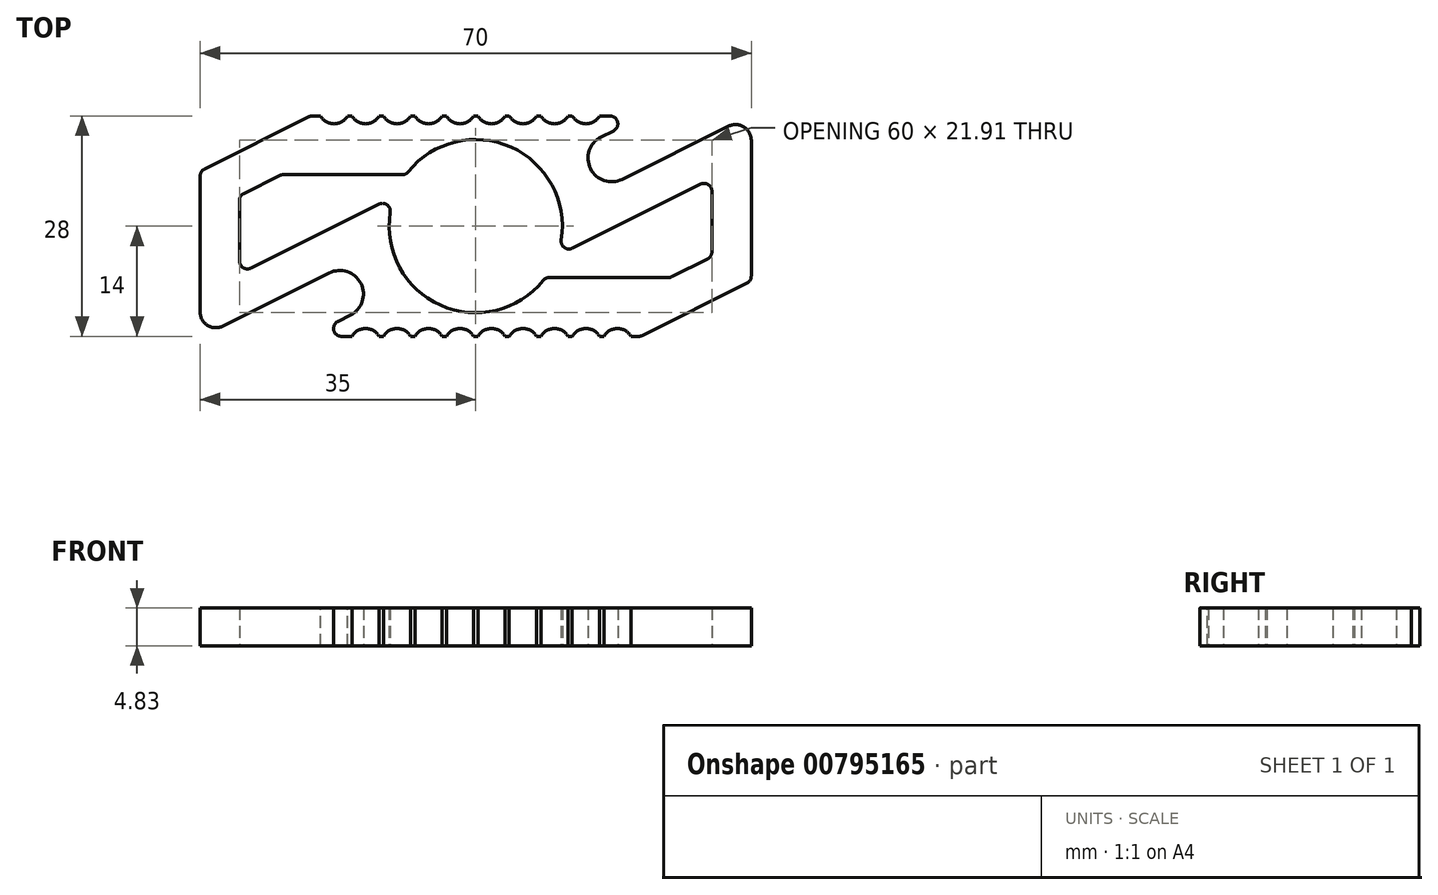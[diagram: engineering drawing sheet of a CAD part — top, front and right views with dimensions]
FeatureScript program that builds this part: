
annotation { "Feature Type Name" : "Feature", "Feature Type Description" : "" }
export const myFeature = defineFeature(function(context is Context, id is Id, definition is map)
    precondition{}
    {
        {
            var Q0;
            Q0=qCreatedBy(makeId("Top.planeOp"),FACE);
            var sketch = newSketch(context, id + "F0", { "sketchPlane" : qUnion([Q0])});
            skArc(sketch, "E0", {"start": v(-10.86, 1.74) * mm, "mid": v(-8.37, -7.14) * mm, "end": v(0, -11) * mm});
            skLineSegment(sketch, "E1.bottom", {"start": v(0, -14) * mm, "end": v(-17.06, -14) * mm});
            skLineSegment(sketch, "E1.top", {"start": v(0, 14) * mm, "end": v(-20.72, 14) * mm});
            skLineSegment(sketch, "E1.right", {"start": v(-35, -10.9) * mm, "end": v(-35, 6.36) * mm});
            skLineSegment(sketch, "E2", {"start": v(0, 29.38) * mm, "end": v(0, -31.46) * mm, "construction": true});
            skLineSegment(sketch, "E3", {"start": v(-17.27, -8.63) * mm, "end": v(-28, -14) * mm});
            skArc(sketch, "E4.0.startCap", {"start": v(-18.6, -5.95) * mm, "mid": v(-14.58, -7.3) * mm, "end": v(-15.93, -11.32) * mm});
            skLineSegment(sketch, "E4.0.left", {"start": v(-15.93, -11.32) * mm, "end": v(-17.5, -12.1) * mm});
            skLineSegment(sketch, "E4.0.right", {"start": v(-18.6, -5.95) * mm, "end": v(-32.1, -12.7) * mm});
            skLineSegment(sketch, "E5.trimOffspring", {"start": v(-34.7, -14) * mm, "end": v(-35, -14) * mm});
            skArc(sketch, "E6.filletArc", {"start": v(-35, -10.9) * mm, "mid": v(-34.05, -12.61) * mm, "end": v(-32.1, -12.7) * mm});
            skPoint(sketch, "E7.visualSharp", {"position": v(-21.3, -14) * mm});
            skArc(sketch, "E7.filletArc", {"start": v(-17.5, -12.1) * mm, "mid": v(-18.03, -13.23) * mm, "end": v(-17.06, -14) * mm});
            skLineSegment(sketch, "E8.0.right", {"start": v(-21.17, 13.9) * mm, "end": v(-34.45, 7.26) * mm});
            skLineSegment(sketch, "E9.3", {"start": v(-24.93, 6.42) * mm, "end": v(-29.45, 4.17) * mm});
            skLineSegment(sketch, "E9.4", {"start": v(-30, -4.44) * mm, "end": v(-30, 3.27) * mm});
            skLineSegment(sketch, "E9.5", {"start": v(-12.3, 2.8) * mm, "end": v(-28.55, -5.33) * mm});
            skPoint(sketch, "E10.visualSharp", {"position": v(-30, 3.89) * mm});
            skArc(sketch, "E10.filletArc", {"start": v(-29.45, 4.17) * mm, "mid": v(-29.85, 3.8) * mm, "end": v(-30, 3.27) * mm});
            skPoint(sketch, "E11.visualSharp", {"position": v(-30, -6.06) * mm});
            skArc(sketch, "E11.filletArc", {"start": v(-30, -4.44) * mm, "mid": v(-29.53, -5.29) * mm, "end": v(-28.55, -5.33) * mm});
            skPoint(sketch, "E12.visualSharp", {"position": v(-19.78, 9) * mm});
            skArc(sketch, "E13.trimOffspring", {"start": v(0, 11) * mm, "mid": v(-4.75, 9.92) * mm, "end": v(-8.56, 6.9) * mm});
            skPoint(sketch, "E14.visualSharp", {"position": v(-35, 6.98) * mm});
            skArc(sketch, "E14.filletArc", {"start": v(-34.45, 7.26) * mm, "mid": v(-34.85, 6.89) * mm, "end": v(-35, 6.36) * mm});
            skLineSegment(sketch, "E15.1.0", {"start": v(21.17, -13.9) * mm, "end": v(34.45, -7.26) * mm});
            skLineSegment(sketch, "E15.1.1", {"start": v(30, 4.44) * mm, "end": v(30, -3.27) * mm});
            skPoint(sketch, "E15.1.2", {"position": v(19.78, -9) * mm});
            skLineSegment(sketch, "E15.1.3", {"start": v(24.93, -6.42) * mm, "end": v(29.45, -4.17) * mm});
            skPoint(sketch, "E15.1.4", {"position": v(35, -6.98) * mm});
            skLineSegment(sketch, "E15.1.5", {"start": v(15.93, 11.32) * mm, "end": v(17.5, 12.1) * mm});
            skLineSegment(sketch, "E15.1.6", {"start": v(18.6, 5.95) * mm, "end": v(32.1, 12.7) * mm});
            skLineSegment(sketch, "E15.1.8", {"start": v(12.3, -2.8) * mm, "end": v(28.55, 5.33) * mm});
            skArc(sketch, "E15.1.9", {"start": v(0, -11) * mm, "mid": v(4.75, -9.92) * mm, "end": v(8.56, -6.9) * mm});
            skArc(sketch, "E15.1.10", {"start": v(18.6, 5.95) * mm, "mid": v(14.58, 7.3) * mm, "end": v(15.93, 11.32) * mm});
            skPoint(sketch, "E15.1.11", {"position": v(30, 6.06) * mm});
            skLineSegment(sketch, "E15.1.12", {"start": v(17.27, 8.63) * mm, "end": v(28, 14) * mm});
            skLineSegment(sketch, "E15.1.13", {"start": v(35, 10.9) * mm, "end": v(35, -6.36) * mm});
            skLineSegment(sketch, "E15.1.15", {"start": v(0, -14) * mm, "end": v(20.72, -14) * mm});
            skLineSegment(sketch, "E15.1.16", {"start": v(0, 14) * mm, "end": v(17.06, 14) * mm});
            skArc(sketch, "E15.1.17", {"start": v(10.86, -1.74) * mm, "mid": v(8.37, 7.14) * mm, "end": v(0, 11) * mm});
            skPoint(sketch, "E15.1.18", {"position": v(21.3, 14) * mm});
            skPoint(sketch, "E15.1.19", {"position": v(30, -3.89) * mm});
            skArc(sketch, "E15.1.20", {"start": v(35, 10.9) * mm, "mid": v(34.05, 12.61) * mm, "end": v(32.1, 12.7) * mm});
            skLineSegment(sketch, "E15.1.21", {"start": v(34.7, 14) * mm, "end": v(35, 14) * mm});
            skArc(sketch, "E15.1.22", {"start": v(30, 4.44) * mm, "mid": v(29.53, 5.29) * mm, "end": v(28.55, 5.33) * mm});
            skArc(sketch, "E15.1.23", {"start": v(17.5, 12.1) * mm, "mid": v(18.03, 13.23) * mm, "end": v(17.06, 14) * mm});
            skArc(sketch, "E15.1.24", {"start": v(29.45, -4.17) * mm, "mid": v(29.85, -3.8) * mm, "end": v(30, -3.27) * mm});
            skArc(sketch, "E15.1.25", {"start": v(34.45, -7.26) * mm, "mid": v(34.85, -6.89) * mm, "end": v(35, -6.36) * mm});
            skPoint(sketch, "E16.visualSharp", {"position": v(-10.33, 3.78) * mm});
            skArc(sketch, "E16.filletArc", {"start": v(-10.86, 1.74) * mm, "mid": v(-11.26, 2.7) * mm, "end": v(-12.3, 2.8) * mm});
            skPoint(sketch, "E17.visualSharp", {"position": v(10.33, -3.78) * mm});
            skArc(sketch, "E17.filletArc", {"start": v(10.86, -1.74) * mm, "mid": v(11.26, -2.7) * mm, "end": v(12.3, -2.8) * mm});
            skPoint(sketch, "E18.visualSharp", {"position": v(6.32, -9) * mm});
            skPoint(sketch, "E19.visualSharp", {"position": v(-6.32, 9) * mm});
            skPoint(sketch, "E20.visualSharp", {"position": v(-20.96, 14) * mm});
            skArc(sketch, "E20.filletArc", {"start": v(-20.72, 14) * mm, "mid": v(-20.95, 13.97) * mm, "end": v(-21.17, 13.9) * mm});
            skPoint(sketch, "E21.visualSharp", {"position": v(20.96, -14) * mm});
            skArc(sketch, "E21.filletArc", {"start": v(20.72, -14) * mm, "mid": v(20.95, -13.97) * mm, "end": v(21.17, -13.9) * mm});
            skLineSegment(sketch, "E22", {"start": v(-24.48, 6.53) * mm, "end": v(-9.34, 6.53) * mm});
            skLineSegment(sketch, "E23", {"start": v(24.48, -6.53) * mm, "end": v(9.34, -6.53) * mm});
            skPoint(sketch, "E12.filletArc.end.orphan", {"position": v(-19.99, 8.9) * mm});
            skPoint(sketch, "E24.visualSharp", {"position": v(-8.85, 6.53) * mm});
            skArc(sketch, "E24.filletArc", {"start": v(-9.34, 6.53) * mm, "mid": v(-8.91, 6.63) * mm, "end": v(-8.56, 6.9) * mm});
            skPoint(sketch, "E25.visualSharp", {"position": v(-24.72, 6.53) * mm});
            skArc(sketch, "E25.filletArc", {"start": v(-24.48, 6.53) * mm, "mid": v(-24.71, 6.5) * mm, "end": v(-24.93, 6.42) * mm});
            skPoint(sketch, "E15.1.26.end.orphan", {"position": v(19.99, -8.9) * mm});
            skPoint(sketch, "E26.visualSharp", {"position": v(8.85, -6.53) * mm});
            skArc(sketch, "E26.filletArc", {"start": v(9.34, -6.53) * mm, "mid": v(8.91, -6.63) * mm, "end": v(8.56, -6.9) * mm});
            skPoint(sketch, "E27.visualSharp", {"position": v(24.72, -6.53) * mm});
            skArc(sketch, "E27.filletArc", {"start": v(24.48, -6.53) * mm, "mid": v(24.71, -6.5) * mm, "end": v(24.93, -6.42) * mm});
            skSolve(sketch);
        }
        {
            var Q0;
            Q0=makeQuery(id+"F0.imprint","IMPRINT",FACE,{"disambiguationData":[TD([[makeQuery(id+"F0.imprint","IMPRINT",EDGE,{"derivedFrom":sQuery(id+"F0.wireOp",EDGE,"E0")}),-1.0]])]});
            extrude(context, id + "F1", {"entities" : qUnion([Q0]), "depth" : 4.83 * mm, "offsetDistance" : 25 * mm});
        }
        {
            var Q0;
            Q0=makeQuery(id+"F1.opExtrude","CAP_FACE",FACE,{"disambiguationData":[OSD([sQuery(id+"F0.wireOp",EDGE,"E0"),sQuery(id+"F0.wireOp",EDGE,"E1.bottom"),sQuery(id+"F0.wireOp",EDGE,"E1.top"),sQuery(id+"F0.wireOp",EDGE,"E1.right"),sQuery(id+"F0.wireOp",EDGE,"E4.0.startCap"),sQuery(id+"F0.wireOp",EDGE,"E4.0.left"),sQuery(id+"F0.wireOp",EDGE,"E4.0.right"),sQuery(id+"F0.wireOp",EDGE,"E6.filletArc"),sQuery(id+"F0.wireOp",EDGE,"E7.filletArc"),sQuery(id+"F0.wireOp",EDGE,"E8.0.right"),sQuery(id+"F0.wireOp",EDGE,"E9.2"),sQuery(id+"F0.wireOp",EDGE,"E9.3"),sQuery(id+"F0.wireOp",EDGE,"E9.4"),sQuery(id+"F0.wireOp",EDGE,"E9.5"),sQuery(id+"F0.wireOp",EDGE,"E10.filletArc"),sQuery(id+"F0.wireOp",EDGE,"E11.filletArc"),sQuery(id+"F0.wireOp",EDGE,"E12.filletArc"),sQuery(id+"F0.wireOp",EDGE,"E13.trimOffspring"),sQuery(id+"F0.wireOp",EDGE,"E14.filletArc"),sQuery(id+"F0.wireOp",EDGE,"E15.1.0"),sQuery(id+"F0.wireOp",EDGE,"E15.1.1"),sQuery(id+"F0.wireOp",EDGE,"E15.1.3"),sQuery(id+"F0.wireOp",EDGE,"E15.1.5"),sQuery(id+"F0.wireOp",EDGE,"E15.1.6"),sQuery(id+"F0.wireOp",EDGE,"E15.1.7"),sQuery(id+"F0.wireOp",EDGE,"E15.1.8"),sQuery(id+"F0.wireOp",EDGE,"E15.1.9"),sQuery(id+"F0.wireOp",EDGE,"E15.1.10"),sQuery(id+"F0.wireOp",EDGE,"E15.1.13"),sQuery(id+"F0.wireOp",EDGE,"E15.1.15"),sQuery(id+"F0.wireOp",EDGE,"E15.1.16"),sQuery(id+"F0.wireOp",EDGE,"E15.1.17"),sQuery(id+"F0.wireOp",EDGE,"E15.1.20"),sQuery(id+"F0.wireOp",EDGE,"E15.1.22"),sQuery(id+"F0.wireOp",EDGE,"E15.1.23"),sQuery(id+"F0.wireOp",EDGE,"E15.1.24"),sQuery(id+"F0.wireOp",EDGE,"E15.1.25"),sQuery(id+"F0.wireOp",EDGE,"E15.1.26"),sQuery(id+"F0.wireOp",EDGE,"E16.filletArc"),sQuery(id+"F0.wireOp",EDGE,"E17.filletArc"),sQuery(id+"F0.wireOp",EDGE,"E18.filletArc"),sQuery(id+"F0.wireOp",EDGE,"E19.filletArc")])],"isStart":false});
            var sketch = newSketch(context, id + "F2", { "sketchPlane" : qUnion([Q0])});
            skLineSegment(sketch, "E28", {"start": v(-18, 15) * mm, "end": v(13.44, 15) * mm, "construction": true});
            skCircle(sketch, "E29", {"center": v(-18, 15) * mm, "radius": 2 * mm});
            skCircle(sketch, "E30.1.0.0", {"center": v(-14, 15) * mm, "radius": 2 * mm});
            skCircle(sketch, "E30.2.0.0", {"center": v(-10, 15) * mm, "radius": 2 * mm});
            skCircle(sketch, "E30.3.0.0", {"center": v(-6, 15) * mm, "radius": 2 * mm});
            skCircle(sketch, "E30.4.0.0", {"center": v(-2, 15) * mm, "radius": 2 * mm});
            skCircle(sketch, "E30.5.0.0", {"center": v(2, 15) * mm, "radius": 2 * mm});
            skCircle(sketch, "E30.6.0.0", {"center": v(6, 15) * mm, "radius": 2 * mm});
            skCircle(sketch, "E30.7.0.0", {"center": v(10, 15) * mm, "radius": 2 * mm});
            skCircle(sketch, "E30.8.0.0", {"center": v(14, 15) * mm, "radius": 2 * mm});
            skLineSegment(sketch, "E30.direction1", {"start": v(-18, 15) * mm, "end": v(-14, 15) * mm, "construction": true});
            skCircle(sketch, "E31.1.0", {"center": v(2, -15) * mm, "radius": 2 * mm});
            skCircle(sketch, "E31.1.1", {"center": v(18, -15) * mm, "radius": 2 * mm});
            skCircle(sketch, "E31.1.2", {"center": v(10, -15) * mm, "radius": 2 * mm});
            skCircle(sketch, "E31.1.3", {"center": v(-2, -15) * mm, "radius": 2 * mm});
            skCircle(sketch, "E31.1.4", {"center": v(-10, -15) * mm, "radius": 2 * mm});
            skLineSegment(sketch, "E31.1.5", {"start": v(18, -15) * mm, "end": v(14, -15) * mm, "construction": true});
            skCircle(sketch, "E31.1.6", {"center": v(-6, -15) * mm, "radius": 2 * mm});
            skCircle(sketch, "E31.1.7", {"center": v(14, -15) * mm, "radius": 2 * mm});
            skLineSegment(sketch, "E31.1.8", {"start": v(18, -15) * mm, "end": v(-13.44, -15) * mm, "construction": true});
            skCircle(sketch, "E31.1.9", {"center": v(-14, -15) * mm, "radius": 2 * mm});
            skCircle(sketch, "E31.1.10", {"center": v(6, -15) * mm, "radius": 2 * mm});
            skPoint(sketch, "E31.center", {"position": v(0, 0) * mm});
            skSolve(sketch);
        }
        {
            var Q0;
            Q0 = qSketchRegion(id + "F2", true);
            extrude(context, id + "F3", {"entities" : qUnion([Q0]), "operationType" : NewBodyOperationType.REMOVE, "oppositeDirection" : true, "depth" : 25 * mm, "offsetDistance" : 25 * mm});
        }
    });
